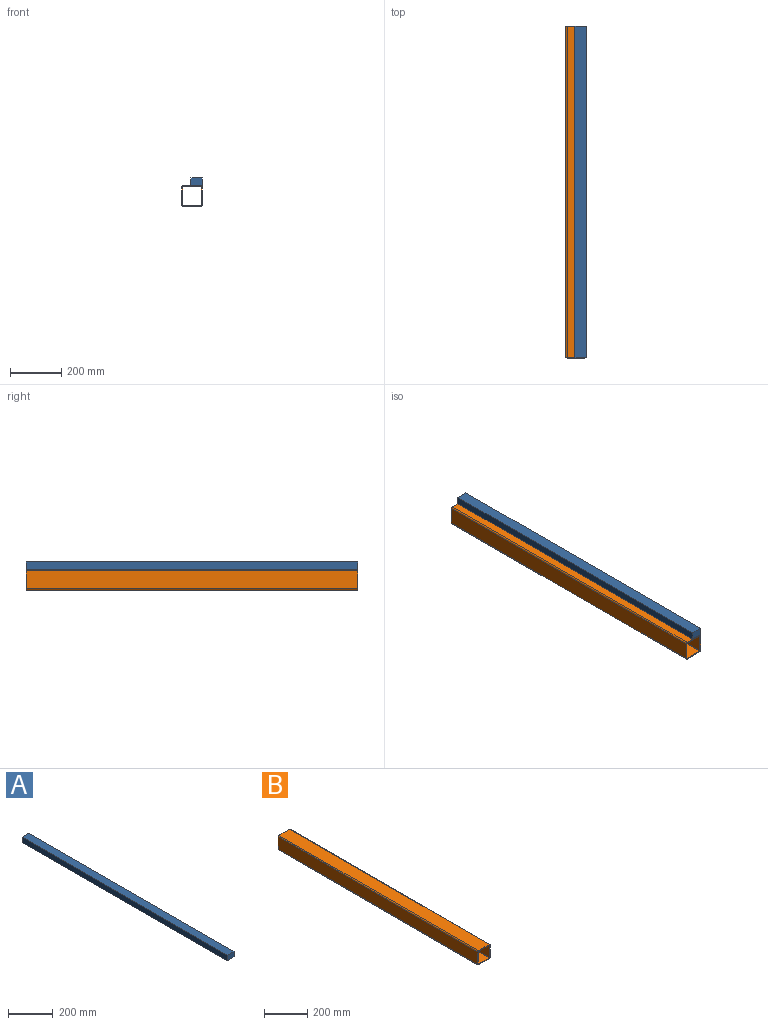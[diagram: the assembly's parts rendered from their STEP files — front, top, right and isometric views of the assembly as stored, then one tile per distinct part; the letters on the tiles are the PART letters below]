
ASSEMBLY  parts=2 mates=1
PART A: 6 faces, bbox 44x1300x30 mm
  f0: plane 1300x30mm, normal (1,0,0), area 39000mm2, adj f1,f3,f4,f5
  f1: plane 1300x44mm, normal (0,0,1), area 57200mm2, adj f0,f2,f4,f5
  f2: plane 1300x30mm, normal (-1,0,0), area 39000mm2, adj f1,f3,f4,f5
  f3: plane 1300x44mm, normal (0,0,-1), area 57200mm2, adj f0,f2,f4,f5
  f4: plane 44x30mm, normal (0,1,0), area 1320mm2, adj f0,f1,f2,f3
  f5: plane 44x30mm, normal (0,-1,0), area 1320mm2, adj f0,f1,f2,f3
PART B: 18 faces, bbox 80x1300x80 mm
  f0: cylinder r=1mm len=1300mm, axis (0,-1,0), area 2042mm2, adj f1,f15,f16,f17
  f1: plane 1300x70mm, normal (-1,0,0), area 91000mm2, adj f0,f2,f16,f17
  f2: cylinder r=1mm len=1300mm, axis (0,-1,0), area 2042mm2, adj f1,f3,f16,f17
  f3: plane 1300x70mm, normal (0,0,1), area 91000mm2, adj f2,f4,f16,f17
  f4: cylinder r=1mm len=1300mm, axis (0,-1,0), area 2042mm2, adj f3,f5,f16,f17
  f5: plane 1300x70mm, normal (1,0,0), area 91000mm2, adj f4,f6,f16,f17
  f6: cylinder r=1mm len=1300mm, axis (0,-1,0), area 2042mm2, adj f5,f15,f16,f17
  f7: plane 1300x70mm, normal (0,0,-1), area 91000mm2, adj f8,f14,f16,f17
  f8: cylinder r=5mm len=1300mm, axis (0,-1,0), area 10210.2mm2, adj f7,f9,f16,f17
  f9: plane 1300x70mm, normal (1,0,0), area 91000mm2, adj f8,f10,f16,f17
  f10: cylinder r=5mm len=1300mm, axis (0,-1,0), area 10210.2mm2, adj f9,f11,f16,f17
  f11: plane 1300x70mm, normal (0,0,1), area 91000mm2, adj f10,f12,f16,f17
  f12: cylinder r=5mm len=1300mm, axis (0,-1,0), area 10210.2mm2, adj f11,f13,f16,f17
  f13: plane 1300x70mm, normal (-1,0,0), area 91000mm2, adj f12,f14,f16,f17
  f14: cylinder r=5mm len=1300mm, axis (0,-1,0), area 10210.2mm2, adj f7,f13,f16,f17
  f15: plane 1300x70mm, normal (0,0,-1), area 91000mm2, adj f0,f6,f16,f17
  f16: plane 80x80mm, normal (0,1,0), area 1195.4mm2, adj f0,f1,f2,f3,f4,f5,f6,f7
  f17: plane 80x80mm, normal (0,-1,0), area 1195.4mm2, adj f0,f1,f2,f3,f4,f5,f6,f7
PLACE A t=(118.1,-369.78,388.64)mm
PLACE B t=(100.1,-369.78,333.64)mm fixed
MATE fastened B.f17 <-> A.f5  axis (0,-1,0) through (100.1,-369.78,373.64)mm
